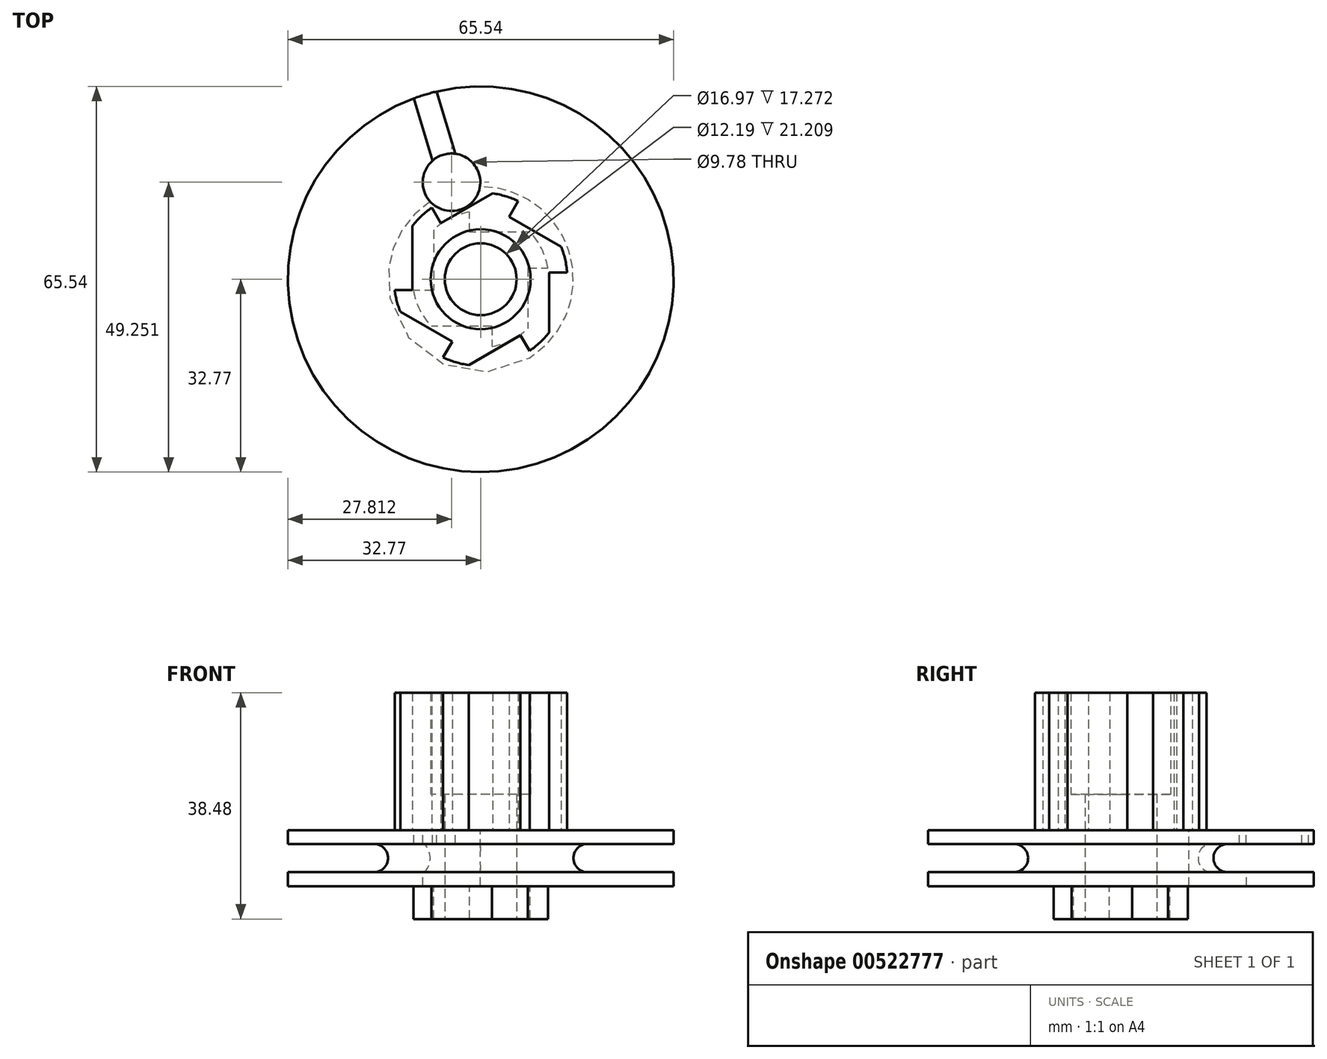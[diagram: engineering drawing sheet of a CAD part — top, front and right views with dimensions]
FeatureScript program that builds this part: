
annotation { "Feature Type Name" : "Feature", "Feature Type Description" : "" }
export const myFeature = defineFeature(function(context is Context, id is Id, definition is map)
    precondition{}
    {
        {
            var Q0;
            Q0=qCreatedBy(makeId("Front.planeOp"),FACE);
            var sketch = newSketch(context, id + "F0", { "sketchPlane" : qUnion([Q0])});
            skLineSegment(sketch, "E0", {"start": v(0, 0) * mm, "end": v(-32.77, 0) * mm});
            skLineSegment(sketch, "E1", {"start": v(-32.77, 0) * mm, "end": v(-32.77, 2.36) * mm});
            skLineSegment(sketch, "E2", {"start": v(-32.77, 9.53) * mm, "end": v(0, 9.53) * mm});
            skLineSegment(sketch, "E3", {"start": v(0, 9.52) * mm, "end": v(0, 0) * mm});
            skLineSegment(sketch, "E4", {"start": v(-32.77, 4.76) * mm, "end": v(0, 4.76) * mm, "construction": true});
            skLineSegment(sketch, "E5", {"start": v(-32.77, 7.16) * mm, "end": v(-18.15, 7.16) * mm});
            skLineSegment(sketch, "E6.MirrorCS", {"start": v(-32.77, 2.36) * mm, "end": v(-18.15, 2.36) * mm});
            skLineSegment(sketch, "E7.trimOffspring", {"start": v(-32.77, 7.16) * mm, "end": v(-32.77, 9.53) * mm});
            skArc(sketch, "E8", {"start": v(-18.15, 2.36) * mm, "mid": v(-15.75, 4.76) * mm, "end": v(-18.15, 7.16) * mm});
            skPoint(sketch, "E9", {"position": v(-15.75, 4.76) * mm});
            skLineSegment(sketch, "E10", {"start": v(0, 0) * mm, "end": v(0, 27.8) * mm, "construction": true});
            skSolve(sketch);
        }
        {
            var Q0;
            Q0 = qSketchRegion(id + "F0", true);
            var Q1;
            Q1 = qConstructionFilter(qBodyType(qCreatedBy(id + "F0" ,EDGE), BodyType.WIRE), ConstructionObject.NO);
            var Q2;
            Q2=sQuery(id+"F0.wireOp",EDGE,"E10");
            revolve(context, id + "F1", {"entities" : qUnion([Q0]), "surfaceEntities" : qUnion([Q1]), "axis" : qUnion([Q2]), "revolveType" : RevolveType.FULL});
        }
        {
            var Q0;
            Q0=qCreatedBy(makeId("Top.planeOp"),FACE);
            var sketch = newSketch(context, id + "F2", { "sketchPlane" : qUnion([Q0])});
            skCircle(sketch, "E11", {"center": v(0, 0) * mm, "radius": 6.1 * mm});
            skCircle(sketch, "E12", {"center": v(0, 0) * mm, "radius": 8.48 * mm});
            skCircle(sketch, "E13", {"center": v(0, 0) * mm, "radius": 11.6 * mm, "construction": true});
            skArc(sketch, "E14", {"start": v(-14.62, -1.85) * mm, "mid": v(-14.26, -3.71) * mm, "end": v(-13.66, -5.52) * mm});
            skLineSegment(sketch, "E15", {"start": v(-11.6, 0) * mm, "end": v(-11.6, 9.07) * mm});
            skLineSegment(sketch, "E16", {"start": v(-11.6, 0) * mm, "end": v(-11.6, -1.85) * mm});
            skLineSegment(sketch, "E17", {"start": v(-11.6, -1.85) * mm, "end": v(-14.62, -1.85) * mm});
            skLineSegment(sketch, "E18", {"start": v(-6.77, 9.5) * mm, "end": v(-5.8, 10.05) * mm});
            skLineSegment(sketch, "E19", {"start": v(-5.8, 10.05) * mm, "end": v(2.05, 14.59) * mm});
            skLineSegment(sketch, "E20", {"start": v(-6.77, 9.5) * mm, "end": v(-8.3, 12.16) * mm});
            skArc(sketch, "E21.trimOffspring", {"start": v(-8.3, 12.16) * mm, "mid": v(-10.08, 10.75) * mm, "end": v(-11.6, 9.07) * mm});
            skLineSegment(sketch, "E22", {"start": v(-6.77, 9.5) * mm, "end": v(-11.6, 6.7) * mm, "construction": true});
            skLineSegment(sketch, "E23", {"start": v(4.84, 10.6) * mm, "end": v(13.66, 5.52) * mm});
            skLineSegment(sketch, "E24", {"start": v(4.84, 10.6) * mm, "end": v(6.38, 13.28) * mm});
            skPoint(sketch, "E25.orphan", {"position": v(0, 13.4) * mm});
            skArc(sketch, "E26.trimOffspring", {"start": v(6.38, 13.28) * mm, "mid": v(4.27, 14.1) * mm, "end": v(2.05, 14.59) * mm});
            skLineSegment(sketch, "E27", {"start": v(11.6, 1.11) * mm, "end": v(11.6, -9.07) * mm});
            skLineSegment(sketch, "E28", {"start": v(11.6, 1.11) * mm, "end": v(14.69, 1.11) * mm});
            skPoint(sketch, "E29.orphan", {"position": v(11.6, 6.7) * mm});
            skArc(sketch, "E30.trimOffspring", {"start": v(14.69, 1.11) * mm, "mid": v(14.34, 3.36) * mm, "end": v(13.66, 5.52) * mm});
            skLineSegment(sketch, "E31", {"start": v(6.77, -9.5) * mm, "end": v(-2.05, -14.59) * mm});
            skLineSegment(sketch, "E32", {"start": v(6.77, -9.5) * mm, "end": v(8.3, -12.16) * mm});
            skPoint(sketch, "E33.orphan", {"position": v(11.6, -6.7) * mm});
            skArc(sketch, "E34.trimOffspring", {"start": v(8.3, -12.16) * mm, "mid": v(10.08, -10.75) * mm, "end": v(11.6, -9.07) * mm});
            skLineSegment(sketch, "E35", {"start": v(-4.84, -10.6) * mm, "end": v(-13.66, -5.52) * mm});
            skLineSegment(sketch, "E36", {"start": v(-4.84, -10.6) * mm, "end": v(-6.38, -13.28) * mm});
            skArc(sketch, "E37.trimOffspring", {"start": v(-6.38, -13.28) * mm, "mid": v(-4.27, -14.1) * mm, "end": v(-2.05, -14.59) * mm});
            skPoint(sketch, "E38.orphan", {"position": v(0, -13.4) * mm});
            skSolve(sketch);
        }
        {
            var Q0;
            Q0 = qSketchRegion(id + "F2", true);
            extrude(context, id + "F3", {"entities" : qUnion([Q0]), "operationType" : NewBodyOperationType.ADD, "depth" : 32.9 * mm, "offsetDistance" : 25.4 * mm});
        }
        {
            var Q0;
            Q0=makeQuery(id+"F2.imprint","IMPRINT",FACE,{"disambiguationData":[TD([[makeQuery(id+"F2.imprint","IMPRINT",EDGE,{"derivedFrom":sQuery(id+"F2.wireOp",EDGE,"E11")}),-1.0]])]});
            var Q1;
            Q1=sQuery(id+"F2.wireOp",EDGE,"E11");
            var Q2;
            Q2=sQuery(id+"F2.wireOp",EDGE,"E12");
            extrude(context, id + "F4", {"entities" : qUnion([Q0]), "operationType" : NewBodyOperationType.ADD, "surfaceEntities" : qUnion([Q1, Q2]), "depth" : 15.62 * mm, "offsetDistance" : 25.4 * mm});
        }
        {
            var Q0;
            Q0=makeQuery(id+"F2.imprint","IMPRINT",FACE,{"disambiguationData":[TD([[makeQuery(id+"F2.imprint","IMPRINT",EDGE,{"derivedFrom":sQuery(id+"F2.wireOp",EDGE,"E11")}),1.0]])]});
            extrude(context, id + "F5", {"entities" : qUnion([Q0]), "operationType" : NewBodyOperationType.REMOVE, "depth" : 25.4 * mm, "offsetDistance" : 25.4 * mm});
        }
        {
            var Q0;
            Q0=makeQuery(id+"F1.opRevolve","SWEPT_FACE",FACE,{"disambiguationData":[OSD([sQuery(id+"F0.wireOp",EDGE,"E0")])]});
            var sketch = newSketch(context, id + "F6", { "sketchPlane" : qUnion([Q0])});
            skCircle(sketch, "E39.0", {"center": v(0, 0) * mm, "radius": 6.1 * mm});
            skCircle(sketch, "E40", {"center": v(0, 0) * mm, "radius": 8.01 * mm, "construction": true});
            skArc(sketch, "E41", {"start": v(-8.01, -8.36) * mm, "mid": v(-5.2, -10.35) * mm, "end": v(-1.92, -11.42) * mm});
            skPoint(sketch, "E42", {"position": v(0, -8.01) * mm});
            skPoint(sketch, "E43", {"position": v(8.01, 0) * mm});
            skPoint(sketch, "E44", {"position": v(0, 8.01) * mm});
            skLineSegment(sketch, "E45", {"start": v(1.92, 8.01) * mm, "end": v(-8.36, 8.01) * mm});
            skLineSegment(sketch, "E46", {"start": v(8.01, -1.92) * mm, "end": v(8.01, 8.36) * mm});
            skPoint(sketch, "E47", {"position": v(-8.01, 0) * mm});
            skLineSegment(sketch, "E48", {"start": v(-8.01, -8.36) * mm, "end": v(-8.01, 1.92) * mm});
            skLineSegment(sketch, "E49", {"start": v(8.36, -8.01) * mm, "end": v(-1.92, -8.01) * mm});
            skLineSegment(sketch, "E50", {"start": v(-8.01, 1.92) * mm, "end": v(-11.42, 1.92) * mm});
            skLineSegment(sketch, "E51", {"start": v(-1.92, -8.01) * mm, "end": v(-1.92, -11.42) * mm});
            skArc(sketch, "E52.trimOffspring", {"start": v(8.36, -8.01) * mm, "mid": v(10.35, -5.2) * mm, "end": v(11.42, -1.92) * mm});
            skPoint(sketch, "E53.orphan", {"position": v(8.01, -8.36) * mm});
            skLineSegment(sketch, "E54", {"start": v(8.01, -1.92) * mm, "end": v(11.42, -1.92) * mm});
            skArc(sketch, "E55.trimOffspring", {"start": v(8.01, 8.36) * mm, "mid": v(5.2, 10.35) * mm, "end": v(1.92, 11.42) * mm});
            skPoint(sketch, "E56.orphan", {"position": v(8.36, 8.01) * mm});
            skLineSegment(sketch, "E57", {"start": v(1.92, 8.01) * mm, "end": v(1.92, 11.42) * mm});
            skArc(sketch, "E58.trimOffspring", {"start": v(-8.36, 8.01) * mm, "mid": v(-10.35, 5.2) * mm, "end": v(-11.42, 1.92) * mm});
            skSolve(sketch);
        }
        {
            var Q0;
            Q0 = qSketchRegion(id + "F6", true);
            extrude(context, id + "F7", {"entities" : qUnion([Q0]), "operationType" : NewBodyOperationType.ADD, "depth" : 5.6 * mm, "offsetDistance" : 25.4 * mm});
        }
        {
            var Q0;
            Q0=makeQuery(id+"F3.boolean.opBoolean","SPLIT",FACE,{"disambiguationData":[TD([makeQuery(id+"F1.opRevolve","SWEPT_FACE",FACE,{"disambiguationData":[OSD([sQuery(id+"F0.wireOp",EDGE,"E7.trimOffspring")])]})])],"derivedFrom":makeQuery(id+"F1.opRevolve","SWEPT_FACE",FACE,{"disambiguationData":[OSD([sQuery(id+"F0.wireOp",EDGE,"E2")])]})});
            var sketch = newSketch(context, id + "F8", { "sketchPlane" : qUnion([Q0])});
            skCircle(sketch, "E59", {"center": v(0, 0) * mm, "radius": 15.75 * mm, "construction": true});
            skCircle(sketch, "E60", {"center": v(-4.96, 16.48) * mm, "radius": 4.89 * mm});
            skLineSegment(sketch, "E61", {"start": v(0, 0) * mm, "end": v(-4.96, 16.48) * mm, "construction": true});
            skLineSegment(sketch, "E62", {"start": v(-4.96, 16.48) * mm, "end": v(-9.44, 31.38) * mm, "construction": true});
            skLineSegment(sketch, "E63", {"start": v(-4.3, 21.32) * mm, "end": v(-7.48, 31.9) * mm});
            skLineSegment(sketch, "E64.MirrorCS", {"start": v(-8.18, 20.15) * mm, "end": v(-11.37, 30.73) * mm});
            skSolve(sketch);
        }
        {
            var Q0;
            Q0 = qSketchRegion(id + "F8", true);
            extrude(context, id + "F9", {"entities" : qUnion([Q0]), "operationType" : NewBodyOperationType.REMOVE, "oppositeDirection" : true, "depth" : 25.4 * mm, "offsetDistance" : 25.4 * mm});
        }
        {
            var Q0;
            {var subQ0=sQuery(id+"F8.wireOp",EDGE,"E63");Q0=makeQuery(id+"F8.imprint","IMPRINT",FACE,{"disambiguationData":[TD([[makeQuery(id+"F8.imprint","IMPRINT",EDGE,{"derivedFrom":subQ0}),1.0]])]});}
            extrude(context, id + "F10", {"entities" : qUnion([Q0]), "operationType" : NewBodyOperationType.REMOVE, "oppositeDirection" : true, "depth" : 4.06 * mm, "offsetDistance" : 25.4 * mm});
        }
    });
